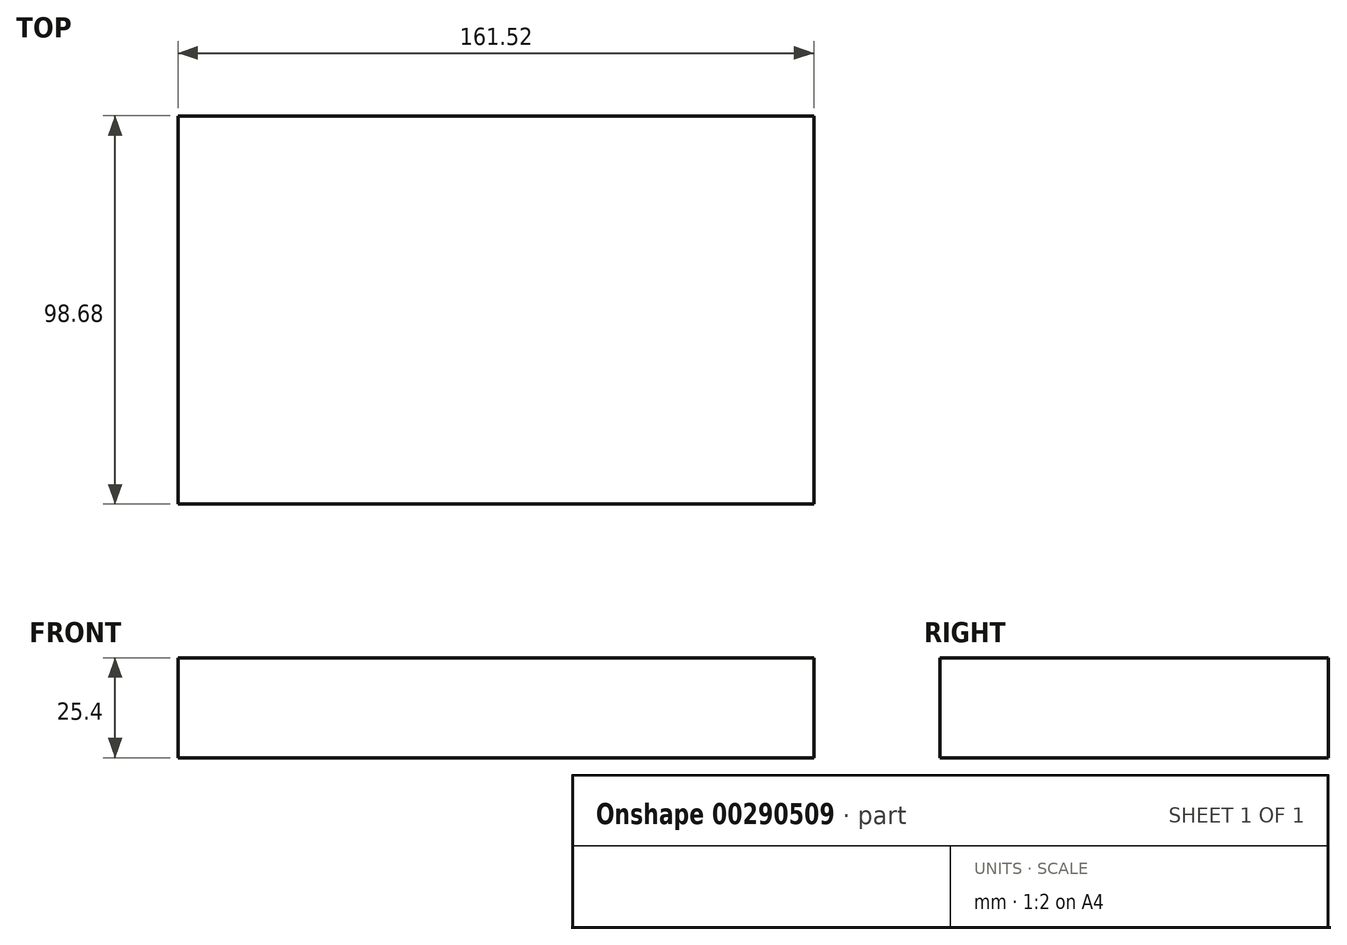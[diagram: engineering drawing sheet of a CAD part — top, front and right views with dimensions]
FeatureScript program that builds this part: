
annotation { "Feature Type Name" : "Feature", "Feature Type Description" : "" }
export const myFeature = defineFeature(function(context is Context, id is Id, definition is map)
    precondition{}
    {
        {
            var Q0;
            Q0=qCreatedBy(makeId("Top.planeOp"),FACE);
            var sketch = newSketch(context, id + "F0", { "sketchPlane" : qUnion([Q0])});
            skLineSegment(sketch, "E0.bottom", {"start": v(80.76, -49.34) * mm, "end": v(-80.76, -49.34) * mm});
            skLineSegment(sketch, "E0.top", {"start": v(80.76, 49.34) * mm, "end": v(-80.76, 49.34) * mm});
            skLineSegment(sketch, "E0.left", {"start": v(80.76, -49.34) * mm, "end": v(80.76, 49.34) * mm});
            skLineSegment(sketch, "E0.right", {"start": v(-80.76, -49.34) * mm, "end": v(-80.76, 49.34) * mm});
            skPoint(sketch, "E0.middle", {"position": v(0, 0) * mm});
            skSolve(sketch);
        }
        {
            var Q0;
            Q0 = qSketchRegion(id + "F0", true);
            extrude(context, id + "F1", {"entities" : qUnion([Q0]), "depth" : 25.4 * mm});
        }
    });
